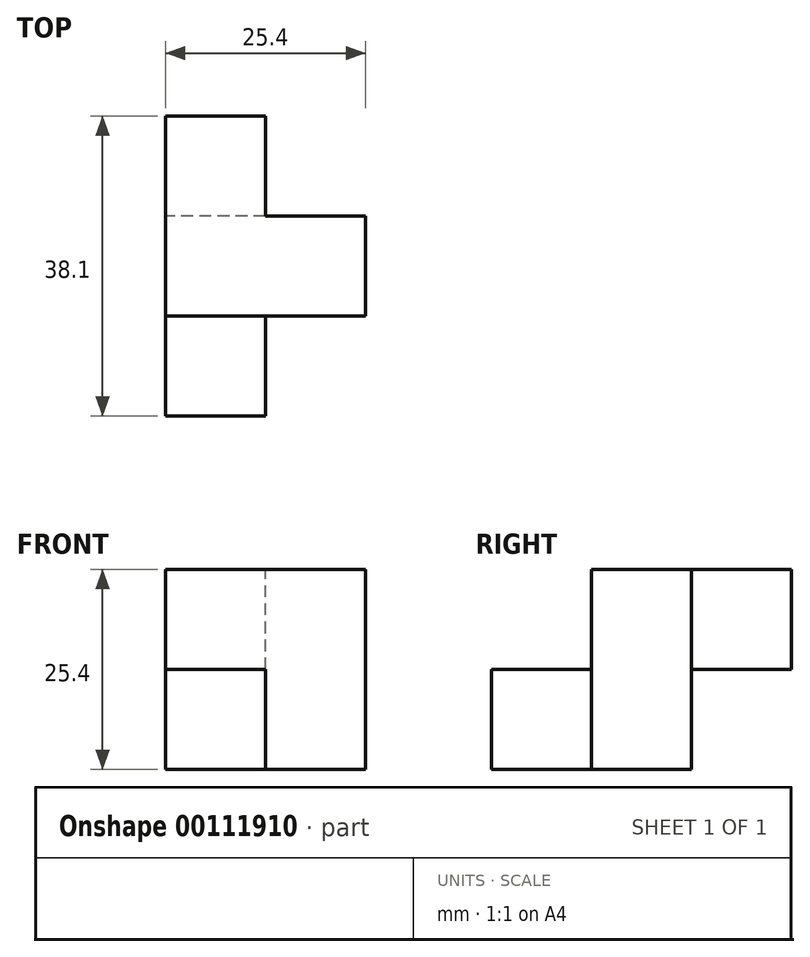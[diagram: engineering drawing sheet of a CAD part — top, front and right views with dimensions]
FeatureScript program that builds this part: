
annotation { "Feature Type Name" : "Feature", "Feature Type Description" : "" }
export const myFeature = defineFeature(function(context is Context, id is Id, definition is map)
    precondition{}
    {
        {
            var Q0;
            Q0=qCreatedBy(makeId("Front.planeOp"),FACE);
            var sketch = newSketch(context, id + "F0", { "sketchPlane" : qUnion([Q0])});
            skLineSegment(sketch, "E0.bottom", {"start": v(-6.65, 16.53) * mm, "end": v(18.75, 16.53) * mm});
            skLineSegment(sketch, "E0.top", {"start": v(-6.65, -8.87) * mm, "end": v(18.75, -8.87) * mm});
            skLineSegment(sketch, "E0.left", {"start": v(-6.65, 16.53) * mm, "end": v(-6.65, -8.87) * mm});
            skLineSegment(sketch, "E0.right", {"start": v(18.75, 16.53) * mm, "end": v(18.75, -8.87) * mm});
            skSolve(sketch);
        }
        {
            var Q0;
            Q0 = qSketchRegion(id + "F0", true);
            extrude(context, id + "F1", {"entities" : qUnion([Q0]), "depth" : 12.7 * mm});
        }
        {
            var Q0;
            Q0=makeQuery(id+"F1.opExtrude","CAP_FACE",FACE,{"disambiguationData":[OSD([sQuery(id+"F0.wireOp",EDGE,"E0.bottom"),sQuery(id+"F0.wireOp",EDGE,"E0.top"),sQuery(id+"F0.wireOp",EDGE,"E0.left"),sQuery(id+"F0.wireOp",EDGE,"E0.right")])],"isStart":false});
            var sketch = newSketch(context, id + "F2", { "sketchPlane" : qUnion([Q0])});
            skLineSegment(sketch, "E1", {"start": v(6.05, -8.87) * mm, "end": v(6.05, 16.53) * mm});
            skLineSegment(sketch, "E2", {"start": v(-6.65, 3.83) * mm, "end": v(18.75, 3.83) * mm});
            skSolve(sketch);
        }
        {
            var Q0;
            Q0 = qSketchRegion(id + "F2", true);
            var Q1;
            {var subQ0=sQuery(id+"F2.wireOp",EDGE,"E1");var subQ1=makeQuery(id+"F1.opExtrude","CAP_EDGE",EDGE,{"disambiguationData":[OSD([sQuery(id+"F0.wireOp",EDGE,"E0.top")])],"isStart":false});var subQ2=makeQuery(id+"F2.imprint","INTERSECT",VERTEX,{"derivedFrom":[subQ1,subQ0]});Q1=makeQuery(id+"F2.imprint","IMPRINT",FACE,{"disambiguationData":[TD([[makeQuery(id+"F2.imprint","IMPRINT",EDGE,{"disambiguationData":[TD([[subQ2,-1.0]])],"derivedFrom":subQ0}),1.0]])]});}
            extrude(context, id + "F3", {"entities" : qUnion([Q0, Q1]), "operationType" : NewBodyOperationType.ADD, "depth" : 12.7 * mm});
        }
        {
            var Q0;
            Q0=makeQuery(id+"F1.opExtrude","CAP_FACE",FACE,{"disambiguationData":[OSD([sQuery(id+"F0.wireOp",EDGE,"E0.bottom"),sQuery(id+"F0.wireOp",EDGE,"E0.top"),sQuery(id+"F0.wireOp",EDGE,"E0.left"),sQuery(id+"F0.wireOp",EDGE,"E0.right")])],"isStart":true});
            var sketch = newSketch(context, id + "F4", { "sketchPlane" : qUnion([Q0])});
            skLineSegment(sketch, "E3", {"start": v(-6.05, -8.87) * mm, "end": v(-6.05, 16.53) * mm});
            skLineSegment(sketch, "E4", {"start": v(-18.75, 3.83) * mm, "end": v(6.65, 3.83) * mm});
            skSolve(sketch);
        }
        {
            var Q0;
            Q0 = qSketchRegion(id + "F4", true);
            var Q1;
            {var subQ0=sQuery(id+"F4.wireOp",EDGE,"E3");var subQ1=makeQuery(id+"F1.opExtrude","CAP_EDGE",EDGE,{"disambiguationData":[OSD([sQuery(id+"F0.wireOp",EDGE,"E0.bottom")])],"isStart":true});var subQ2=makeQuery(id+"F4.imprint","INTERSECT",VERTEX,{"derivedFrom":[subQ1,subQ0]});Q1=makeQuery(id+"F4.imprint","IMPRINT",FACE,{"disambiguationData":[TD([[makeQuery(id+"F4.imprint","IMPRINT",EDGE,{"disambiguationData":[TD([[subQ2,1.0]])],"derivedFrom":subQ0}),-1.0]])]});}
            extrude(context, id + "F5", {"entities" : qUnion([Q0, Q1]), "operationType" : NewBodyOperationType.ADD, "depth" : 12.7 * mm});
        }
    });
